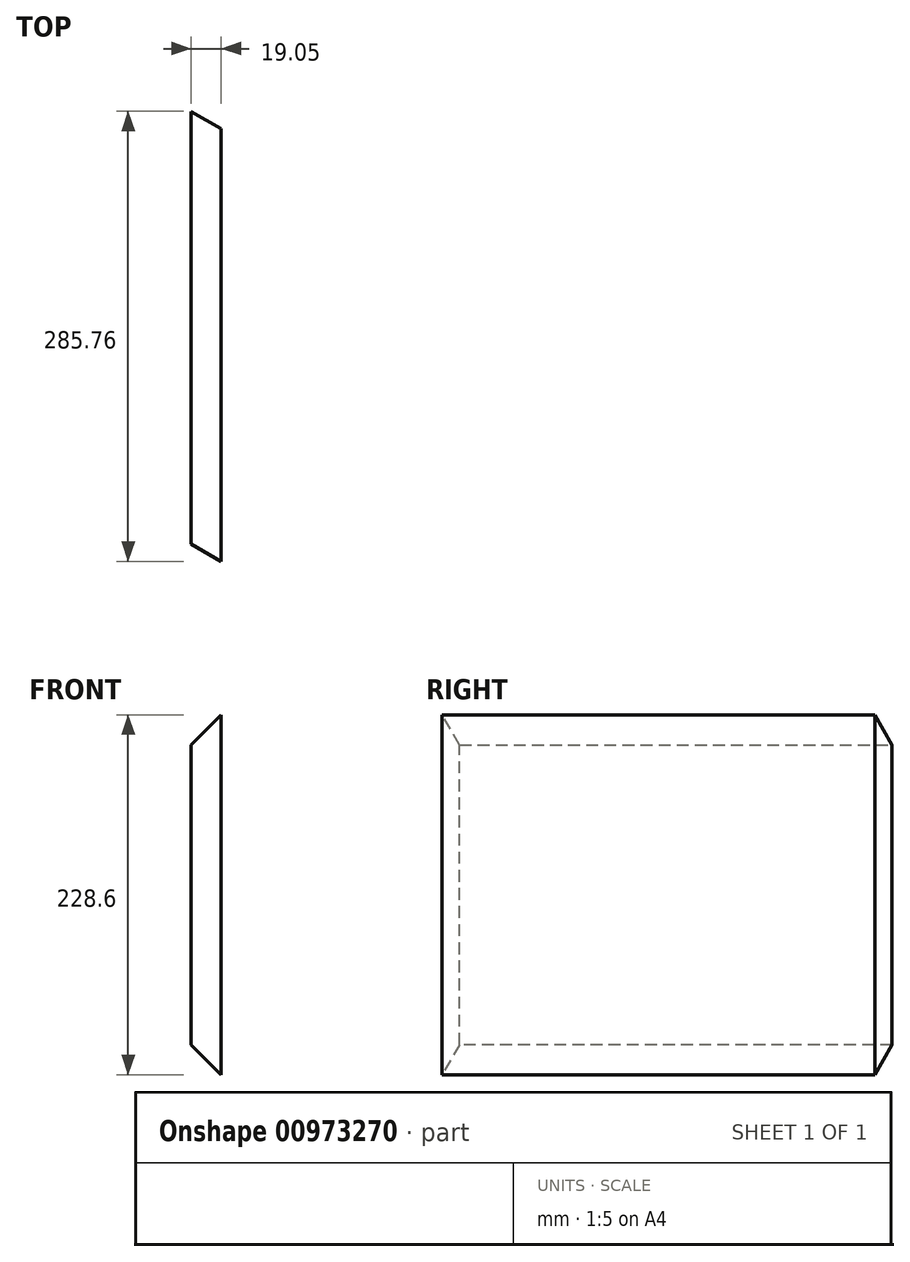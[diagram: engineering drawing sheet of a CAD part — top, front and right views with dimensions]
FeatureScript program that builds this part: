
annotation { "Feature Type Name" : "Feature", "Feature Type Description" : "" }
export const myFeature = defineFeature(function(context is Context, id is Id, definition is map)
    precondition{}
    {
        {
            var Q0;
            Q0=qCreatedBy(makeId("Right.planeOp"),FACE);
            var sketch = newSketch(context, id + "F0", { "sketchPlane" : qUnion([Q0])});
            skLineSegment(sketch, "E0.bottom", {"start": v(142.88, -114.3) * mm, "end": v(-142.88, -114.3) * mm});
            skLineSegment(sketch, "E0.top", {"start": v(142.88, 114.3) * mm, "end": v(-142.87, 114.3) * mm});
            skLineSegment(sketch, "E0.left", {"start": v(142.88, -114.3) * mm, "end": v(142.88, 114.3) * mm});
            skLineSegment(sketch, "E0.right", {"start": v(-142.88, -114.3) * mm, "end": v(-142.87, 114.3) * mm});
            skPoint(sketch, "E0.middle", {"position": v(0, 0) * mm});
            skSolve(sketch);
        }
        {
            var Q0;
            Q0=makeQuery(id+"F0.imprint","IMPRINT",FACE,{"disambiguationData":[TD([[makeQuery(id+"F0.imprint","IMPRINT",EDGE,{"derivedFrom":sQuery(id+"F0.wireOp",EDGE,"E0.bottom")}),-1.0]])]});
            extrude(context, id + "F1", {"entities" : qUnion([Q0]), "depth" : 19.05 * mm, "offsetDistance" : 25.4 * mm});
        }
        {
            var Q0;
            Q0=makeQuery(id+"F1.opExtrude","SWEPT_FACE",FACE,{"disambiguationData":[OSD([sQuery(id+"F0.wireOp",EDGE,"E0.top")])]});
            var sketch = newSketch(context, id + "F2", { "sketchPlane" : qUnion([Q0])});
            skLineSegment(sketch, "E1", {"start": v(19.05, -142.87) * mm, "end": v(0, -131.88) * mm});
            skLineSegment(sketch, "E2", {"start": v(0, -131.88) * mm, "end": v(0, -142.87) * mm});
            skLineSegment(sketch, "E3", {"start": v(0, -142.87) * mm, "end": v(19.05, -142.87) * mm});
            skLineSegment(sketch, "E4", {"start": v(0, 142.88) * mm, "end": v(19.05, 131.88) * mm});
            skLineSegment(sketch, "E5", {"start": v(19.05, 131.88) * mm, "end": v(19.05, 142.88) * mm});
            skLineSegment(sketch, "E6", {"start": v(19.05, 142.88) * mm, "end": v(0, 142.88) * mm});
            skSolve(sketch);
        }
        {
            var Q0;
            Q0=qSketchRegion(id+"F2",true);
            extrude(context, id + "F3", {"entities" : qUnion([Q0]), "operationType" : NewBodyOperationType.REMOVE, "endBound" : BoundingType.THROUGH_ALL, "oppositeDirection" : true, "depth" : 25.4 * mm, "offsetDistance" : 25.4 * mm});
        }
        {
            var Q0;
            Q0=makeQuery(id+"F1.opExtrude","CAP_EDGE",EDGE,{"disambiguationData":[OSD([sQuery(id+"F0.wireOp",EDGE,"E0.top")])],"isStart":true});
            var Q1;
            Q1=makeQuery(id+"F1.opExtrude","CAP_EDGE",EDGE,{"disambiguationData":[OSD([sQuery(id+"F0.wireOp",EDGE,"E0.bottom")])],"isStart":true});
            chamfer(context, id + "F4", {"entities" : qUnion([Q0, Q1]), "width" : 19.05 * mm, "tangentPropagation" : true});
        }
    });
